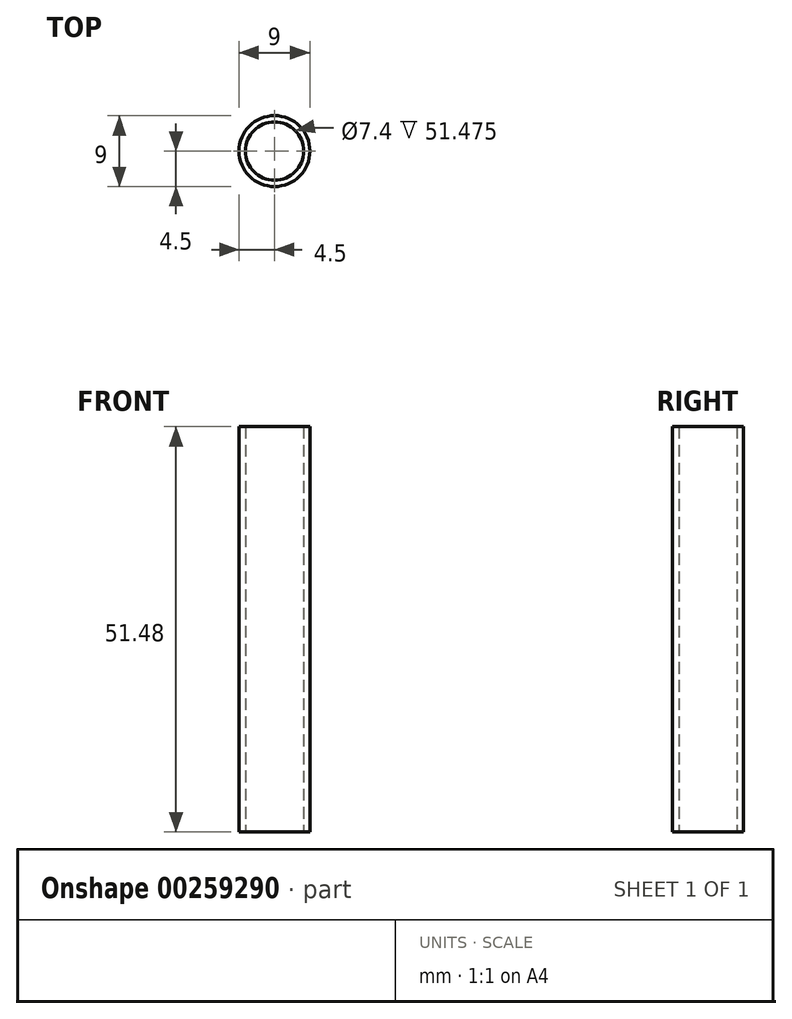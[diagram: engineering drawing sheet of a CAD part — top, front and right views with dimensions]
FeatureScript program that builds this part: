
annotation { "Feature Type Name" : "Feature", "Feature Type Description" : "" }
export const myFeature = defineFeature(function(context is Context, id is Id, definition is map)
    precondition{}
    {
        {
            var Q0;
            Q0=qCreatedBy(makeId("Top.planeOp"),FACE);
            var sketch = newSketch(context, id + "F0", { "sketchPlane" : qUnion([Q0])});
            skCircle(sketch, "E0", {"center": v(0, 0) * mm, "radius": 3.7 * mm});
            skCircle(sketch, "E1", {"center": v(0, 0) * mm, "radius": 4.5 * mm});
            skSolve(sketch);
        }
        {
            var Q0;
            Q0=makeQuery(id+"F0.imprint","IMPRINT",FACE,{"disambiguationData":[TD([[makeQuery(id+"F0.imprint","IMPRINT",EDGE,{"derivedFrom":sQuery(id+"F0.wireOp",EDGE,"E0")}),-1.0]])]});
            extrude(context, id + "F1", {"entities" : qUnion([Q0]), "depth" : 53.97 * mm});
        }
        {
            var Q0;
            Q0=makeQuery(id+"F1.opExtrude","CAP_FACE",FACE,{"disambiguationData":[OSD([sQuery(id+"F0.wireOp",EDGE,"E0"),sQuery(id+"F0.wireOp",EDGE,"E1")])],"isStart":false});
            extrude(context, id + "F2", {"entities" : qUnion([Q0]), "operationType" : NewBodyOperationType.REMOVE, "oppositeDirection" : true, "depth" : 2.5 * mm});
        }
    });
